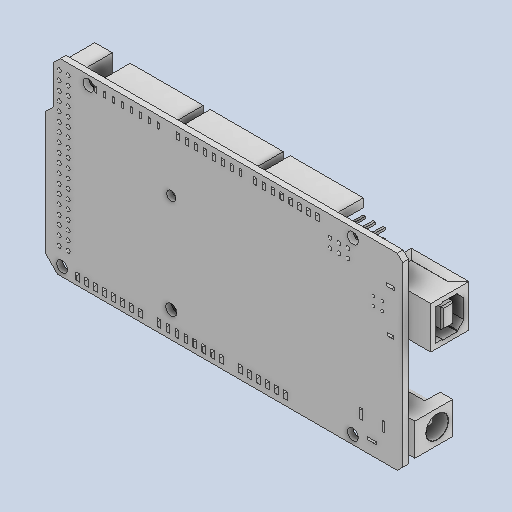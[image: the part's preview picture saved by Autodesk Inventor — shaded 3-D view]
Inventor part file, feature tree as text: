
AUTODESK INVENTOR PART (.ipt)
format: ipt  version: 2024 (Build 280153000, 153)  size: 1,226,752 bytes
history: native  units: in
note: dims shown in document units (in); Inventor stores cm internally (conversion verified against a paired STEP export)
features: fillet x1
ambient origin geometry x8: Origin, YZ Plane, XZ Plane, XY Plane, X Axis, Y Axis, Z Axis, Center Point
bodies: Solid1 (feature_tree)
feature tree (1):
  fillet  "Fillet5"  [1 undecoded]
note: 1 required parameter value undecoded (feature->parameter linkage not recoverable at this tier; creation-order binding heuristic only, values carry confidence <= 0.55)
